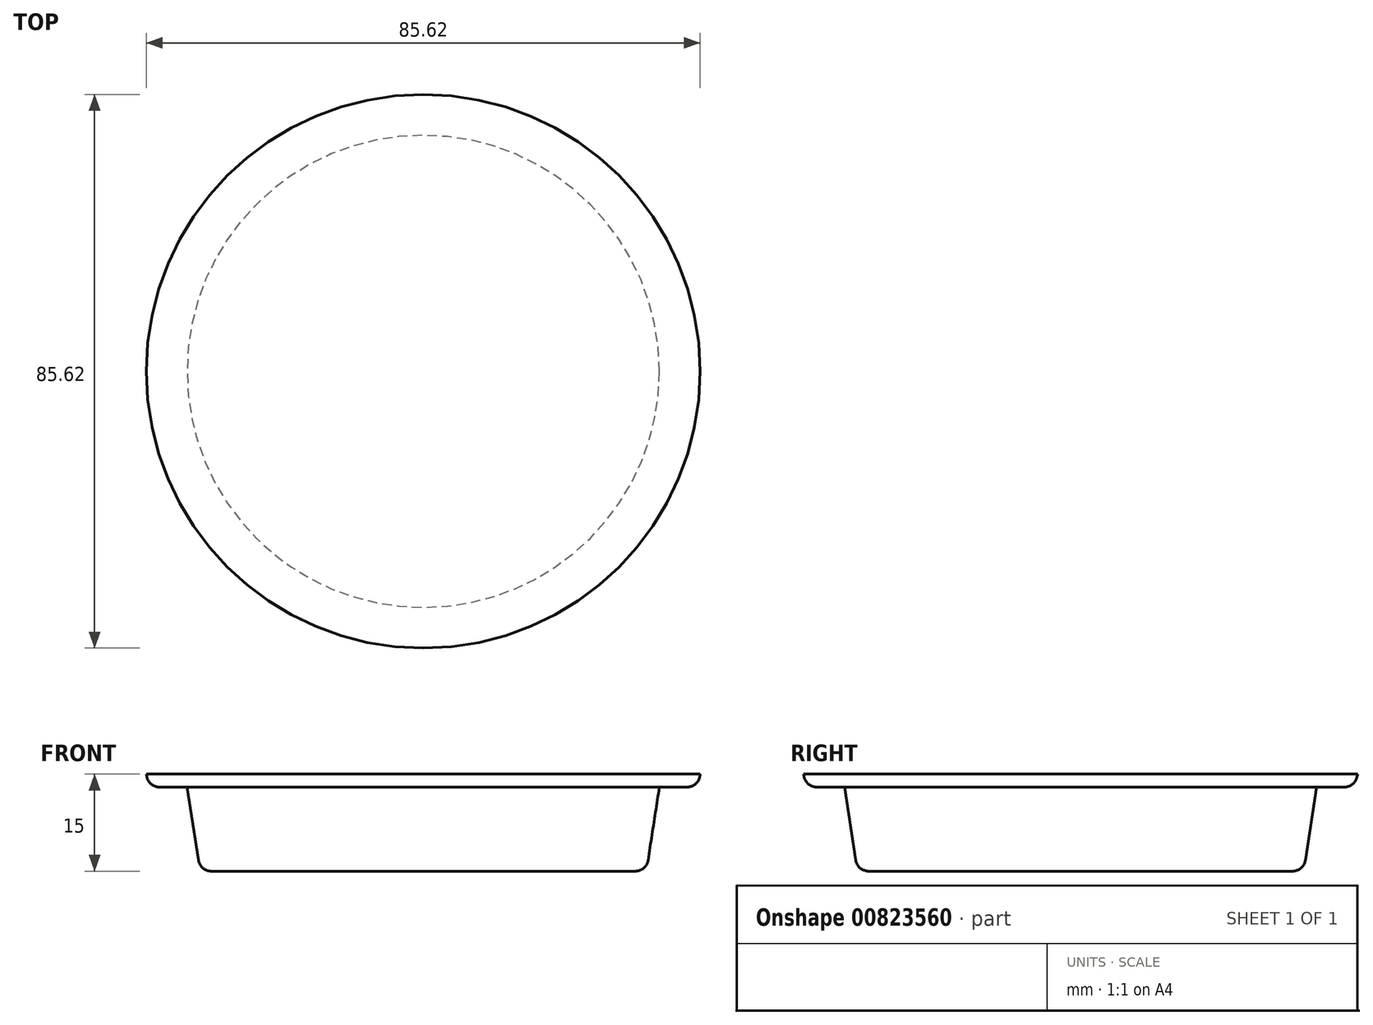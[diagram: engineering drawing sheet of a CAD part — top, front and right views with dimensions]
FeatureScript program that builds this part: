
annotation { "Feature Type Name" : "Feature", "Feature Type Description" : "" }
export const myFeature = defineFeature(function(context is Context, id is Id, definition is map)
    precondition{}
    {
        {
            var Q0;
            Q0=qCreatedBy(makeId("Top.planeOp"),FACE);
            var sketch = newSketch(context, id + "F0", { "sketchPlane" : qUnion([Q0])});
            skCircle(sketch, "E0", {"center": v(0, 0) * mm, "radius": 34.5 * mm});
            skSolve(sketch);
        }
        {
            var Q0;
            Q0=qSketchRegion(id+"F0",true);
            extrude(context, id + "F1", {"entities" : qUnion([Q0]), "depth" : 13 * mm, "offsetDistance" : 25 * mm, "hasDraft" : true, "draftAngle" : 8.75 * degree});
        }
        {
            var Q0;
            Q0=makeQuery(id+"F1.opExtrude","CAP_FACE",FACE,{"disambiguationData":[OSD([sQuery(id+"F0.wireOp",EDGE,"E0")])],"isStart":false});
            var sketch = newSketch(context, id + "F2", { "sketchPlane" : qUnion([Q0])});
            skCircle(sketch, "E1", {"center": v(0, 0) * mm, "radius": 42.5 * mm});
            skSolve(sketch);
        }
        {
            var Q0;
            Q0=qSketchRegion(id+"F2",true);
            extrude(context, id + "F3", {"entities" : qUnion([Q0]), "operationType" : NewBodyOperationType.ADD, "depth" : 2 * mm, "offsetDistance" : 25 * mm, "hasDraft" : true, "draftAngle" : 8.7 * degree});
        }
        {
            var Q0;
            Q0=makeQuery(id+"F1.opExtrude","CAP_EDGE",EDGE,{"disambiguationData":[OSD([sQuery(id+"F0.wireOp",EDGE,"E0")])],"isStart":true});
            var Q1;
            Q1=makeQuery(id+"F1.opExtrude","CAP_EDGE",EDGE,{"disambiguationData":[OSD([sQuery(id+"F0.wireOp",EDGE,"E0")])],"isStart":false});
            var Q2;
            Q2=makeQuery(id+"F3.opExtrude","CAP_EDGE",EDGE,{"disambiguationData":[OSD([sQuery(id+"F2.wireOp",EDGE,"E1")])],"isStart":true});
            fillet(context, id + "F4", {"entities" : qUnion([Q0, Q1, Q2]), "radius" : 2 * mm, "tangentPropagation" : true, "allowEdgeOverflow" : false});
        }
    });
